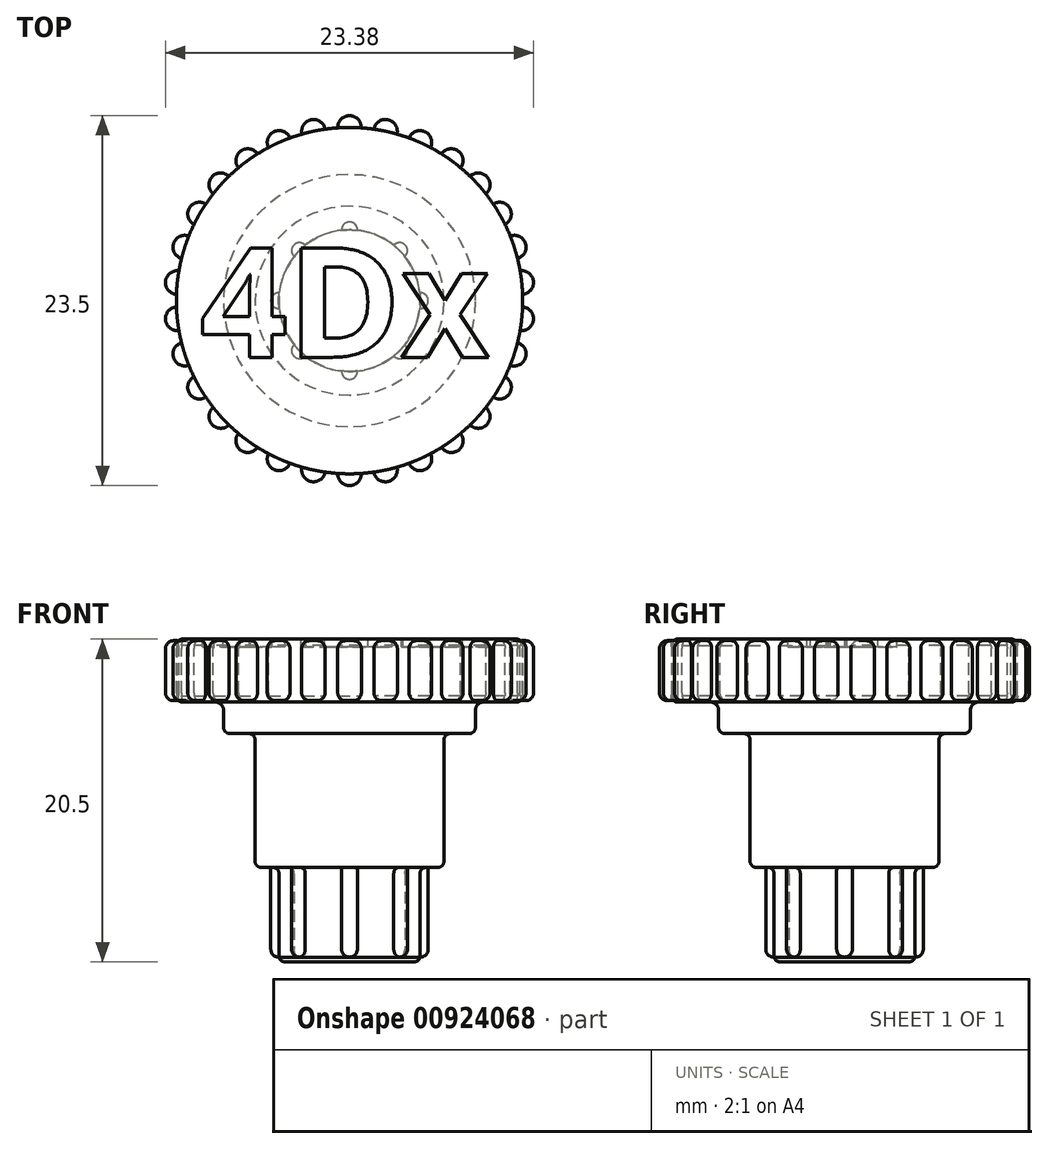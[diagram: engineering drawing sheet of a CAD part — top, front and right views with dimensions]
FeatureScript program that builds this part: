
annotation { "Feature Type Name" : "Feature", "Feature Type Description" : "" }
export const myFeature = defineFeature(function(context is Context, id is Id, definition is map)
    precondition{}
    {
        {
            var Q0;
            Q0=qCreatedBy(makeId("Front.planeOp"),FACE);
            var sketch = newSketch(context, id + "F0", { "sketchPlane" : qUnion([Q0])});
            skLineSegment(sketch, "E0", {"start": v(0, 0) * mm, "end": v(0, 20.5) * mm});
            skLineSegment(sketch, "E1", {"start": v(0, 20.5) * mm, "end": v(11, 20.5) * mm});
            skLineSegment(sketch, "E2", {"start": v(11, 20.5) * mm, "end": v(11, 16.5) * mm});
            skLineSegment(sketch, "E3", {"start": v(11, 16.5) * mm, "end": v(8, 16.5) * mm});
            skLineSegment(sketch, "E4", {"start": v(8, 16.5) * mm, "end": v(8, 14.5) * mm});
            skLineSegment(sketch, "E5", {"start": v(8, 14.5) * mm, "end": v(6, 14.5) * mm});
            skLineSegment(sketch, "E6", {"start": v(6, 14.5) * mm, "end": v(6, 6) * mm});
            skLineSegment(sketch, "E7", {"start": v(6, 6) * mm, "end": v(4.5, 6) * mm});
            skLineSegment(sketch, "E8", {"start": v(4.5, 6) * mm, "end": v(4.5, 0) * mm});
            skLineSegment(sketch, "E9", {"start": v(4.5, 0) * mm, "end": v(0, 0) * mm});
            skSolve(sketch);
        }
        {
            var Q0;
            Q0=makeQuery(id+"F0.imprint","IMPRINT",FACE,{"disambiguationData":[TD([[makeQuery(id+"F0.imprint","IMPRINT",EDGE,{"derivedFrom":sQuery(id+"F0.wireOp",EDGE,"E0")}),-1.0]])]});
            var Q1;
            Q1=sQuery(id+"F0.wireOp",EDGE,"E0");
            revolve(context, id + "F1", {"surfaceOperationType" : NewSurfaceOperationType.NEW, "entities" : qUnion([Q0]), "axis" : qUnion([Q1]), "revolveType" : RevolveType.FULL});
        }
        {
            var Q0;
            Q0=makeQuery(id+"F1.opRevolve","SWEPT_EDGE",EDGE,{"disambiguationData":[OSD([sQuery(id+"F0.wireOp",EDGE,"E3"),sQuery(id+"F0.wireOp",EDGE,"E4")])]});
            fillet(context, id + "F2", {"entities" : qUnion([Q0]), "radius" : 0.5 * mm, "tangentPropagation" : true, "allowEdgeOverflow" : false});
        }
        {
            var Q0;
            Q0=makeQuery(id+"F1.opRevolve","SWEPT_EDGE",EDGE,{"disambiguationData":[OSD([sQuery(id+"F0.wireOp",EDGE,"E2"),sQuery(id+"F0.wireOp",EDGE,"E3")])]});
            var Q1;
            Q1=makeQuery(id+"F1.opRevolve","SWEPT_EDGE",EDGE,{"disambiguationData":[OSD([sQuery(id+"F0.wireOp",EDGE,"E1"),sQuery(id+"F0.wireOp",EDGE,"E2")])]});
            fillet(context, id + "F3", {"entities" : qUnion([Q0, Q1]), "radius" : 0.4 * mm, "tangentPropagation" : true, "allowEdgeOverflow" : false});
        }
        {
            var Q0;
            Q0=makeQuery(id+"F1.opRevolve","SWEPT_FACE",FACE,{"disambiguationData":[OSD([sQuery(id+"F0.wireOp",EDGE,"E1")])]});
            cPlane(context, id + "F4", {"entities" : qUnion([Q0]), "cplaneType" : CPlaneType.OFFSET, "offset" : 0 * mm, "width" : 150 * mm, "height" : 150 * mm});
        }
        {
            var Q0;
            Q0=qCreatedBy(id+"F4.planeOp",FACE);
            var sketch = newSketch(context, id + "F5", { "sketchPlane" : qUnion([Q0])});
            skText(sketch, "E10", { "text": "4Dx", "fontName": "OpenSans-Bold.ttf"});
            const initialGuessF5  = {"E10": [-0.00949, -0.0036, 1, 0, 0.007]};
            skSetInitialGuess(sketch, initialGuessF5);
            skSolve(sketch);
        }
        {
            var Q0;
            Q0=qCreatedBy(id+"F4.planeOp",FACE);
            var sketch = newSketch(context, id + "F6", { "sketchPlane" : qUnion([Q0])});
            skCircle(sketch, "E11", {"center": v(0, 0) * mm, "radius": 11 * mm});
            skArc(sketch, "E12", {"start": v(-0.75, -10.97) * mm, "mid": v(0, -11.75) * mm, "end": v(0.75, -10.97) * mm});
            skSolve(sketch);
        }
        {
            var Q0;
            {var subQ0=sQuery(id+"F6.wireOp",EDGE,"E12");Q0=makeQuery(id+"F6.imprint","IMPRINT",FACE,{"disambiguationData":[TD([[makeQuery(id+"F6.imprint","IMPRINT",EDGE,{"derivedFrom":subQ0}),1.0]])]});}
            extrude(context, id + "F7", {"entities" : qUnion([Q0]), "operationType" : NewBodyOperationType.ADD, "oppositeDirection" : true, "depth" : 3.91 * mm, "offsetDistance" : 25 * mm, "hasSecondDirection" : true, "secondDirectionOppositeDirection" : true, "secondDirectionDepth" : 0.1 * mm});
        }
        {
            var Q0;
            Q0=makeQuery(id+"F7.opExtrude","CAP_EDGE",EDGE,{"disambiguationData":[OSD([sQuery(id+"F6.wireOp",EDGE,"E12")])],"isStart":true});
            var Q1;
            Q1=makeQuery(id+"F7.opExtrude","CAP_EDGE",EDGE,{"disambiguationData":[OSD([sQuery(id+"F6.wireOp",EDGE,"E12")])],"isStart":false});
            fillet(context, id + "F8", {"entities" : qUnion([Q0, Q1]), "radius" : 0.5 * mm, "tangentPropagation" : true, "allowEdgeOverflow" : false});
        }
        {
            var Q0;
            Q0=makeQuery(id+"F1.opRevolve","SWEPT_BODY",BODY,{"disambiguationData":[OSD([sQuery(id+"F0.wireOp",EDGE,"E0"),sQuery(id+"F0.wireOp",EDGE,"E1"),sQuery(id+"F0.wireOp",EDGE,"E2"),sQuery(id+"F0.wireOp",EDGE,"E3"),sQuery(id+"F0.wireOp",EDGE,"E4"),sQuery(id+"F0.wireOp",EDGE,"E5"),sQuery(id+"F0.wireOp",EDGE,"E6"),sQuery(id+"F0.wireOp",EDGE,"E7"),sQuery(id+"F0.wireOp",EDGE,"E8"),sQuery(id+"F0.wireOp",EDGE,"E9")])]});
            var Q1;
            Q1=makeQuery(id+"F1.opRevolve","SWEPT_FACE",FACE,{"disambiguationData":[OSD([sQuery(id+"F0.wireOp",EDGE,"E2")])]});
            circularPattern(context, id + "F9", {"operationType" : NewBodyOperationType.ADD, "entities" : qUnion([Q0]), "axis" : qUnion([Q1]), "angle" : 360 * degree, "instanceCount" : 30, "equalSpace" : true, "computeTransformsWithoutBuiltin" : true});
        }
        {
            var Q0;
            Q0=makeQuery(id+"F1.opRevolve","SWEPT_EDGE",EDGE,{"disambiguationData":[OSD([sQuery(id+"F0.wireOp",EDGE,"E6"),sQuery(id+"F0.wireOp",EDGE,"E7")])]});
            var Q1;
            Q1=makeQuery(id+"F1.opRevolve","SWEPT_EDGE",EDGE,{"disambiguationData":[OSD([sQuery(id+"F0.wireOp",EDGE,"E7"),sQuery(id+"F0.wireOp",EDGE,"E8")])]});
            var Q2;
            Q2=makeQuery(id+"F1.opRevolve","SWEPT_EDGE",EDGE,{"disambiguationData":[OSD([sQuery(id+"F0.wireOp",EDGE,"E5"),sQuery(id+"F0.wireOp",EDGE,"E6")])]});
            var Q3;
            Q3=makeQuery(id+"F1.opRevolve","SWEPT_EDGE",EDGE,{"disambiguationData":[OSD([sQuery(id+"F0.wireOp",EDGE,"E4"),sQuery(id+"F0.wireOp",EDGE,"E5")])]});
            var Q4;
            Q4=makeQuery(id+"F1.opRevolve","SWEPT_EDGE",EDGE,{"disambiguationData":[OSD([sQuery(id+"F0.wireOp",EDGE,"E8"),sQuery(id+"F0.wireOp",EDGE,"E9")])]});
            fillet(context, id + "F10", {"entities" : qUnion([Q0, Q1, Q2, Q3, Q4]), "radius" : 0.4 * mm, "tangentPropagation" : true, "allowEdgeOverflow" : false});
        }
        {
            var Q0;
            Q0=makeQuery(id+"F1.opRevolve","SWEPT_FACE",FACE,{"disambiguationData":[OSD([sQuery(id+"F0.wireOp",EDGE,"E9")])]});
            cPlane(context, id + "F11", {"entities" : qUnion([Q0]), "cplaneType" : CPlaneType.OFFSET, "offset" : 0.3 * mm, "oppositeDirection" : true, "width" : 150 * mm, "height" : 150 * mm});
        }
        {
            var Q0;
            Q0=qCreatedBy(id+"F11.planeOp",FACE);
            var sketch = newSketch(context, id + "F12", { "sketchPlane" : qUnion([Q0])});
            skArc(sketch, "E13", {"start": v(-0.5, 4.47) * mm, "mid": v(0, -4.5) * mm, "end": v(0.5, 4.47) * mm});
            skArc(sketch, "E14", {"start": v(0.5, 4.47) * mm, "mid": v(0, 5) * mm, "end": v(-0.5, 4.47) * mm});
            skArc(sketch, "E15.1.0", {"start": v(-2.8, 3.52) * mm, "mid": v(-3.54, 3.54) * mm, "end": v(-3.52, 2.8) * mm});
            skArc(sketch, "E15.2.0", {"start": v(-4.47, 0.5) * mm, "mid": v(-5, 0) * mm, "end": v(-4.47, -0.5) * mm});
            skArc(sketch, "E15.3.0", {"start": v(-3.52, -2.8) * mm, "mid": v(-3.54, -3.54) * mm, "end": v(-2.8, -3.52) * mm});
            skArc(sketch, "E15.4.0", {"start": v(-0.5, -4.47) * mm, "mid": v(0, -5) * mm, "end": v(0.5, -4.47) * mm});
            skArc(sketch, "E15.5.0", {"start": v(2.8, -3.52) * mm, "mid": v(3.54, -3.54) * mm, "end": v(3.52, -2.8) * mm});
            skArc(sketch, "E15.6.0", {"start": v(4.47, -0.5) * mm, "mid": v(5, 0) * mm, "end": v(4.47, 0.5) * mm});
            skArc(sketch, "E15.7.0", {"start": v(3.52, 2.8) * mm, "mid": v(3.54, 3.54) * mm, "end": v(2.8, 3.52) * mm});
            skSolve(sketch);
        }
        {
            var Q0;
            Q0=qSketchRegion(id+"F12",true);
            extrude(context, id + "F13", {"entities" : qUnion([Q0]), "operationType" : NewBodyOperationType.ADD, "oppositeDirection" : true, "depth" : 7 * mm, "offsetDistance" : 25 * mm});
        }
        {
            var Q0;
            Q0=makeQuery(id+"F13.opExtrude","CAP_EDGE",EDGE,{"disambiguationData":[OSD([sQuery(id+"F12.wireOp",EDGE,"E15.7.0")])],"isStart":true});
            var Q1;
            Q1=makeQuery(id+"F13.opExtrude","CAP_EDGE",EDGE,{"disambiguationData":[OSD([sQuery(id+"F12.wireOp",EDGE,"E15.6.0")])],"isStart":true});
            var Q2;
            Q2=makeQuery(id+"F13.opExtrude","CAP_EDGE",EDGE,{"disambiguationData":[OSD([sQuery(id+"F12.wireOp",EDGE,"E15.5.0")])],"isStart":true});
            var Q3;
            Q3=makeQuery(id+"F13.opExtrude","CAP_EDGE",EDGE,{"disambiguationData":[OSD([sQuery(id+"F12.wireOp",EDGE,"E14")])],"isStart":true});
            var Q4;
            Q4=makeQuery(id+"F13.opExtrude","CAP_EDGE",EDGE,{"disambiguationData":[OSD([sQuery(id+"F12.wireOp",EDGE,"E15.1.0")])],"isStart":true});
            var Q5;
            Q5=makeQuery(id+"F13.opExtrude","CAP_EDGE",EDGE,{"disambiguationData":[OSD([sQuery(id+"F12.wireOp",EDGE,"E15.4.0")])],"isStart":true});
            var Q6;
            Q6=makeQuery(id+"F13.opExtrude","CAP_EDGE",EDGE,{"disambiguationData":[OSD([sQuery(id+"F12.wireOp",EDGE,"E15.3.0")])],"isStart":true});
            var Q7;
            Q7=makeQuery(id+"F13.opExtrude","CAP_EDGE",EDGE,{"disambiguationData":[OSD([sQuery(id+"F12.wireOp",EDGE,"E15.2.0")])],"isStart":true});
            fillet(context, id + "F14", {"entities" : qUnion([Q0, Q1, Q2, Q3, Q4, Q5, Q6, Q7]), "radius" : 0.5 * mm, "tangentPropagation" : true, "allowEdgeOverflow" : false});
        }
        {
            var Q0;
            Q0 = qSketchRegion(id + "F5", true);
            extrude(context, id + "F15", {"entities" : qUnion([Q0]), "operationType" : NewBodyOperationType.REMOVE, "oppositeDirection" : true, "depth" : 0.5 * mm, "offsetDistance" : 25 * mm});
        }
    });
